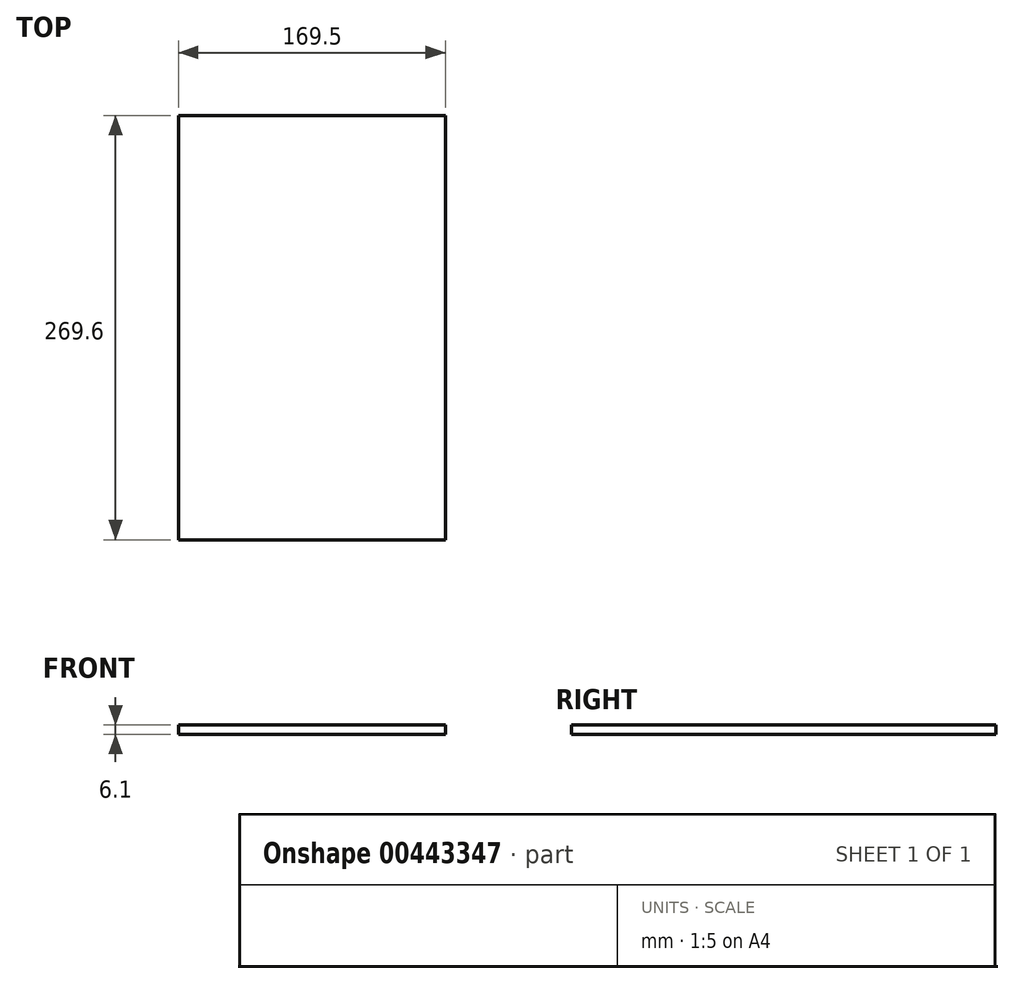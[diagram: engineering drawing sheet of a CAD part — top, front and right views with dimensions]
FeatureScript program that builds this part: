
annotation { "Feature Type Name" : "Feature", "Feature Type Description" : "" }
export const myFeature = defineFeature(function(context is Context, id is Id, definition is map)
    precondition{}
    {
        {
            var Q0;
            Q0=qCreatedBy(makeId("Top.planeOp"),FACE);
            var sketch = newSketch(context, id + "F0", { "sketchPlane" : qUnion([Q0])});
            skLineSegment(sketch, "E0.bottom", {"start": v(84.75, -134.8) * mm, "end": v(-84.75, -134.8) * mm});
            skLineSegment(sketch, "E0.top", {"start": v(84.75, 134.8) * mm, "end": v(-84.75, 134.8) * mm});
            skLineSegment(sketch, "E0.left", {"start": v(84.75, -134.8) * mm, "end": v(84.75, 134.8) * mm});
            skLineSegment(sketch, "E0.right", {"start": v(-84.75, -134.8) * mm, "end": v(-84.75, 134.8) * mm});
            skPoint(sketch, "E0.middle", {"position": v(0, 0) * mm});
            skSolve(sketch);
        }
        {
            var Q0;
            Q0 = qSketchRegion(id + "F0", true);
            extrude(context, id + "F1", {"entities" : qUnion([Q0]), "depth" : 6.1 * mm});
        }
    });
